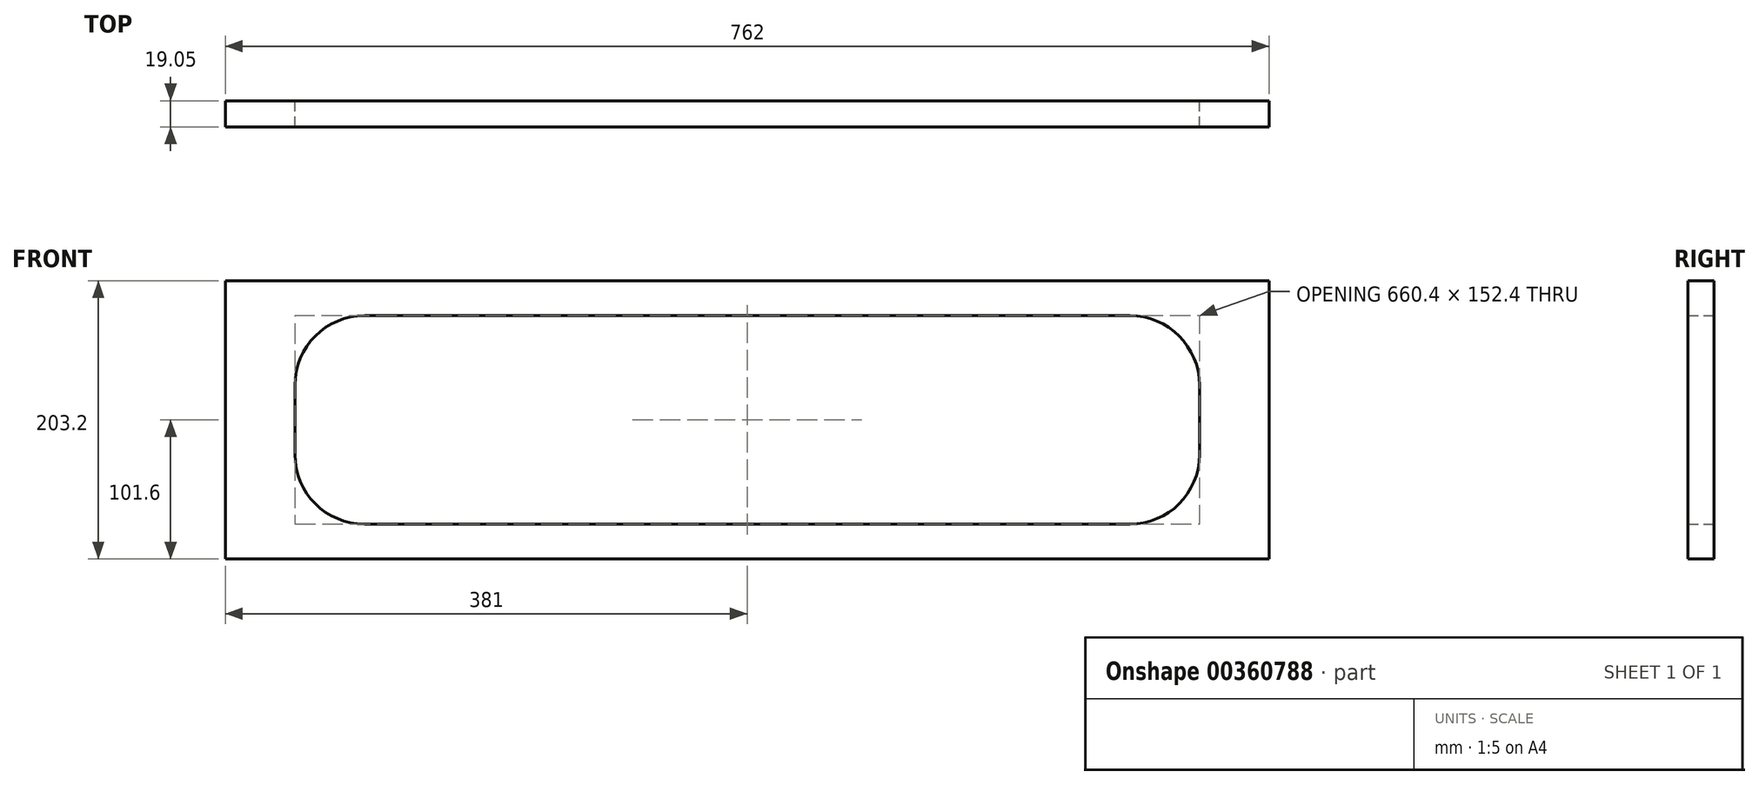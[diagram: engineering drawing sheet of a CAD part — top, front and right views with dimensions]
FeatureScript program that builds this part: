
annotation { "Feature Type Name" : "Feature", "Feature Type Description" : "" }
export const myFeature = defineFeature(function(context is Context, id is Id, definition is map)
    precondition{}
    {
        {
            var Q0;
            Q0=qCreatedBy(makeId("Front.planeOp"),FACE);
            var sketch = newSketch(context, id + "F0", { "sketchPlane" : qUnion([Q0])});
            skLineSegment(sketch, "E0.bottom", {"start": v(0, 0) * mm, "end": v(762, 0) * mm});
            skLineSegment(sketch, "E0.top", {"start": v(0, 203.2) * mm, "end": v(762, 203.2) * mm});
            skLineSegment(sketch, "E0.left", {"start": v(0, 0) * mm, "end": v(0, 203.2) * mm});
            skLineSegment(sketch, "E0.right", {"start": v(762, 0) * mm, "end": v(762, 203.2) * mm});
            skLineSegment(sketch, "E1.bottom", {"start": v(101.6, 177.8) * mm, "end": v(660.4, 177.8) * mm});
            skLineSegment(sketch, "E1.top", {"start": v(101.6, 25.4) * mm, "end": v(660.4, 25.4) * mm});
            skLineSegment(sketch, "E1.left", {"start": v(50.8, 127) * mm, "end": v(50.8, 76.2) * mm});
            skLineSegment(sketch, "E1.right", {"start": v(711.2, 127) * mm, "end": v(711.2, 76.2) * mm});
            skPoint(sketch, "E2.visualSharp", {"position": v(50.8, 177.8) * mm});
            skArc(sketch, "E2.filletArc", {"start": v(101.6, 177.8) * mm, "mid": v(65.68, 162.92) * mm, "end": v(50.8, 127) * mm});
            skPoint(sketch, "E3.visualSharp", {"position": v(50.8, 25.4) * mm});
            skArc(sketch, "E3.filletArc", {"start": v(50.8, 76.2) * mm, "mid": v(65.68, 40.28) * mm, "end": v(101.6, 25.4) * mm});
            skPoint(sketch, "E4.visualSharp", {"position": v(711.2, 177.8) * mm});
            skArc(sketch, "E4.filletArc", {"start": v(711.2, 127) * mm, "mid": v(696.32, 162.92) * mm, "end": v(660.4, 177.8) * mm});
            skPoint(sketch, "E5.visualSharp", {"position": v(711.2, 25.4) * mm});
            skArc(sketch, "E5.filletArc", {"start": v(660.4, 25.4) * mm, "mid": v(696.32, 40.28) * mm, "end": v(711.2, 76.2) * mm});
            skSolve(sketch);
        }
        {
            var Q0;
            Q0=makeQuery(id+"F0.imprint","IMPRINT",FACE,{"disambiguationData":[TD([[makeQuery(id+"F0.imprint","IMPRINT",EDGE,{"derivedFrom":sQuery(id+"F0.wireOp",EDGE,"E0.bottom")}),1.0]])]});
            extrude(context, id + "F1", {"entities" : qUnion([Q0]), "depth" : 19.05 * mm});
        }
    });
